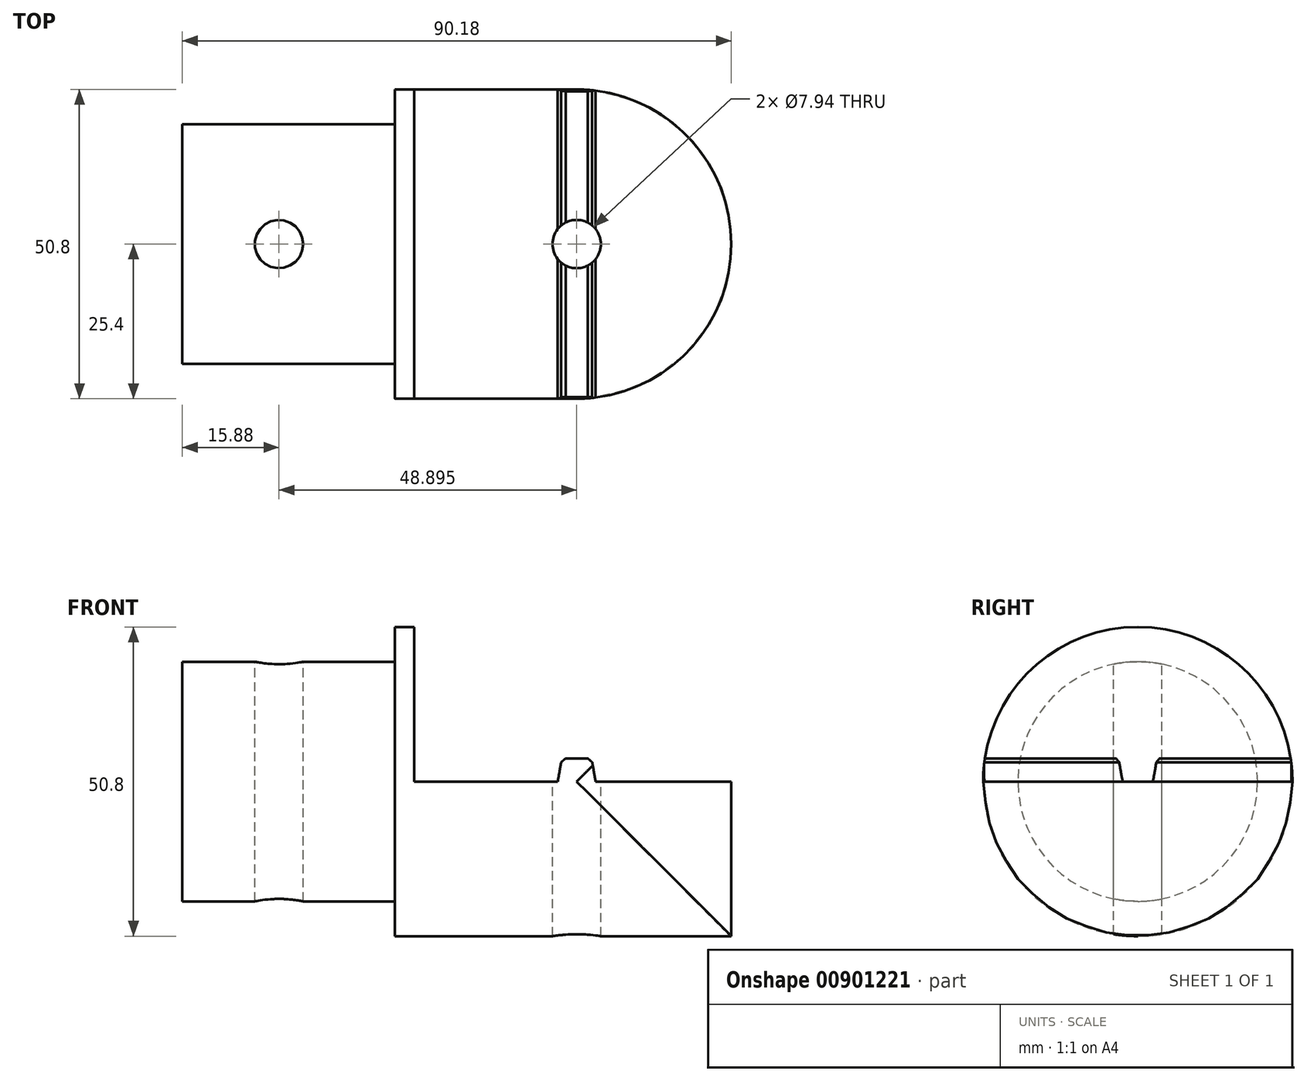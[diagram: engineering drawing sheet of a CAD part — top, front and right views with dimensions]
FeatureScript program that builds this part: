
annotation { "Feature Type Name" : "Feature", "Feature Type Description" : "" }
export const myFeature = defineFeature(function(context is Context, id is Id, definition is map)
    precondition{}
    {
        {
            var Q0;
            Q0=qCreatedBy(makeId("Right.planeOp"),FACE);
            var sketch = newSketch(context, id + "F0", { "sketchPlane" : qUnion([Q0])});
            skCircle(sketch, "E0", {"center": v(0, 0) * mm, "radius": 25.4 * mm});
            skSolve(sketch);
        }
        {
            var Q0;
            Q0=makeQuery(id+"F0.imprint","IMPRINT",FACE,{"disambiguationData":[TD([[makeQuery(id+"F0.imprint","IMPRINT",EDGE,{"derivedFrom":sQuery(id+"F0.wireOp",EDGE,"E0")}),1.0]])]});
            var Q1;
            Q1=sQuery(id+"F0.wireOp",EDGE,"E0");
            extrude(context, id + "F1", {"entities" : qUnion([Q0]), "surfaceEntities" : qUnion([Q1]), "depth" : 3.17 * mm, "offsetDistance" : 25.4 * mm});
        }
        {
            var Q0;
            Q0=makeQuery(id+"F1.opExtrude","CAP_FACE",FACE,{"disambiguationData":[OSD([sQuery(id+"F0.wireOp",EDGE,"E0")])],"isStart":false});
            var sketch = newSketch(context, id + "F2", { "sketchPlane" : qUnion([Q0])});
            skCircle(sketch, "E1", {"center": v(0, 0) * mm, "radius": 19.69 * mm});
            skSolve(sketch);
        }
        {
            var Q0;
            Q0=qSketchRegion(id+"F2",true);
            extrude(context, id + "F3", {"entities" : qUnion([Q0]), "operationType" : NewBodyOperationType.ADD, "oppositeDirection" : true, "depth" : 38.1 * mm, "offsetDistance" : 25.4 * mm});
        }
        {
            var Q0;
            Q0=qCreatedBy(makeId("Right.planeOp"),FACE);
            var sketch = newSketch(context, id + "F4", { "sketchPlane" : qUnion([Q0])});
            skArc(sketch, "E2.0", {"start": v(-25.4, 0) * mm, "mid": v(0, -25.4) * mm, "end": v(25.4, 0) * mm});
            skLineSegment(sketch, "E3", {"start": v(-25.4, 0) * mm, "end": v(25.4, 0) * mm});
            skSolve(sketch);
        }
        {
            var Q0;
            Q0 = qSketchRegion(id + "F4", true);
            extrude(context, id + "F5", {"entities" : qUnion([Q0]), "operationType" : NewBodyOperationType.ADD, "depth" : 58.42 * mm, "offsetDistance" : 25.4 * mm});
        }
        {
            var Q0;
            Q0=makeQuery(id+"F1.opExtrude","CAP_FACE",FACE,{"disambiguationData":[OSD([sQuery(id+"F0.wireOp",EDGE,"E0")])],"isStart":false});
            cPlane(context, id + "F6", {"entities" : qUnion([Q0]), "cplaneType" : CPlaneType.OFFSET, "offset" : 26.67 * mm, "width" : 152.4 * mm, "height" : 152.4 * mm});
        }
        {
            var Q0;
            Q0=qCreatedBy(makeId("Front.planeOp"),FACE);
            var sketch = newSketch(context, id + "F7", { "sketchPlane" : qUnion([Q0])});
            skLineSegment(sketch, "E4", {"start": v(29.84, 54.74) * mm, "end": v(29.85, -54.74) * mm, "construction": true});
            skLineSegment(sketch, "E5.left", {"start": v(32.96, 0) * mm, "end": v(26.73, 0) * mm});
            skLineSegment(sketch, "E5.right", {"start": v(32.28, 3.81) * mm, "end": v(27.4, 3.81) * mm});
            skLineSegment(sketch, "E6", {"start": v(32.96, 0) * mm, "end": v(32.28, 3.8) * mm});
            skLineSegment(sketch, "E7", {"start": v(26.73, 0) * mm, "end": v(27.4, 3.8) * mm});
            skSolve(sketch);
        }
        {
            var Q0;
            Q0=qSketchRegion(id+"F7",true);
            var Q1;
            Q1=makeQuery(id+"F1GSwWC16j8S8zG_1.boolean.opBoolean","MERGE",FACE,{"derivedFrom":[makeQuery(id+"F1.opExtrude","CAP_FACE",FACE,{"disambiguationData":[OSD([sQuery(id+"F0.wireOp",EDGE,"E0")])],"isStart":false})],"fromTools":[makeQuery(id+"F1GSwWC16j8S8zG_1.opExtrude","SWEPT_FACE",FACE,{"disambiguationData":[OSD([sQuery(id+"Fo2Aks5cWjRStkX_1.wireOp",EDGE,"LD30eS7f-A7DZ-0PzW-ksg2-Q8TgDjSmhPE0.left")])]})]});
            extrude(context, id + "F8", {"entities" : qUnion([Q0]), "operationType" : NewBodyOperationType.ADD, "endBound" : BoundingType.SYMMETRIC, "oppositeDirection" : true, "depth" : 50.8 * mm, "endBoundEntityFace" : qUnion([Q1]), "offsetDistance" : 25.4 * mm});
        }
        {
            var Q0;
            Q0=makeQuery(id+"F1.opExtrude","CAP_FACE",FACE,{"disambiguationData":[OSD([sQuery(id+"F0.wireOp",EDGE,"E0")])],"isStart":false});
            var sketch = newSketch(context, id + "F9", { "sketchPlane" : qUnion([Q0])});
            skArc(sketch, "E8", {"start": v(25.4, 0) * mm, "mid": v(0, 25.4) * mm, "end": v(-25.4, 0) * mm});
            skLineSegment(sketch, "E9", {"start": v(-25.4, 0) * mm, "end": v(-30.5, 0) * mm});
            skLineSegment(sketch, "E10", {"start": v(-30.5, 0) * mm, "end": v(-30.5, 28.85) * mm});
            skLineSegment(sketch, "E11", {"start": v(-30.5, 28.85) * mm, "end": v(30.5, 28.85) * mm});
            skLineSegment(sketch, "E12", {"start": v(30.5, 28.85) * mm, "end": v(30.5, 0) * mm});
            skLineSegment(sketch, "E13", {"start": v(25.4, 0) * mm, "end": v(30.5, 0) * mm});
            skSolve(sketch);
        }
        {
            var Q0;
            Q0 = qSketchRegion(id + "F9", true);
            extrude(context, id + "F10", {"entities" : qUnion([Q0]), "operationType" : NewBodyOperationType.REMOVE, "depth" : 50.8 * mm, "offsetDistance" : 25.4 * mm});
        }
        {
            var Q0;
            Q0=makeQuery(id+"F8.opExtrude","SWEPT_EDGE",EDGE,{"disambiguationData":[OSD([sQuery(id+"F7.wireOp",EDGE,"E5.right"),sQuery(id+"F7.wireOp",EDGE,"E6")])]});
            var Q1;
            Q1=makeQuery(id+"F8.opExtrude","SWEPT_EDGE",EDGE,{"disambiguationData":[OSD([sQuery(id+"F7.wireOp",EDGE,"E5.right"),sQuery(id+"F7.wireOp",EDGE,"E7")])]});
            chamfer(context, id + "F11", {"entities" : qUnion([Q0, Q1]), "width" : 0.76 * mm});
        }
        {
            var Q0;
            Q0=qCreatedBy(makeId("Top.planeOp"),FACE);
            cPlane(context, id + "F12", {"entities" : qUnion([Q0]), "cplaneType" : CPlaneType.OFFSET, "offset" : 25.4 * mm, "width" : 152.4 * mm, "height" : 152.4 * mm});
        }
        {
            var Q0;
            Q0=qCreatedBy(id+"F12.planeOp",FACE);
            var sketch = newSketch(context, id + "F13", { "sketchPlane" : qUnion([Q0])});
            skPoint(sketch, "E14", {"position": v(29.85, 0) * mm});
            skPoint(sketch, "E15", {"position": v(29.84, 25.4) * mm});
            skPoint(sketch, "E16", {"position": v(29.85, -25.4) * mm});
            skArc(sketch, "E17", {"start": v(29.85, -25.4) * mm, "mid": v(55.25, 0) * mm, "end": v(29.85, 25.4) * mm});
            skLineSegment(sketch, "E18", {"start": v(29.85, -25.4) * mm, "end": v(29.85, -30.23) * mm});
            skLineSegment(sketch, "E19", {"start": v(29.85, -30.23) * mm, "end": v(58.42, -30.23) * mm});
            skLineSegment(sketch, "E20", {"start": v(58.42, -30.23) * mm, "end": v(58.42, 31.14) * mm});
            skLineSegment(sketch, "E21", {"start": v(58.42, 31.14) * mm, "end": v(29.84, 31.14) * mm});
            skLineSegment(sketch, "E22", {"start": v(29.84, 31.14) * mm, "end": v(29.84, 25.4) * mm});
            skLineSegment(sketch, "E23", {"start": v(29.84, 33.97) * mm, "end": v(29.85, -31.5) * mm, "construction": true});
            skSolve(sketch);
        }
        {
            var Q0;
            Q0=qSketchRegion(id+"F13",true);
            extrude(context, id + "F14", {"entities" : qUnion([Q0]), "operationType" : NewBodyOperationType.REMOVE, "endBound" : BoundingType.THROUGH_ALL, "oppositeDirection" : true, "depth" : 25.4 * mm, "offsetDistance" : 25.4 * mm});
        }
        {
            var Q0;
            Q0=qCreatedBy(id+"F12.planeOp",FACE);
            var sketch = newSketch(context, id + "F15", { "sketchPlane" : qUnion([Q0])});
            skPoint(sketch, "E24", {"position": v(29.85, 0) * mm});
            skPoint(sketch, "E25", {"position": v(-19.05, 0) * mm});
            skSolve(sketch);
        }
        {
            var Q0;
            Q0=sQuery(id+"F15.wireOp",VERTEX,"E25");
            var Q1;
            Q1=sQuery(id+"F15.wireOp",VERTEX,"E24");
            var Q2;
            Q2=makeQuery(id+"F1.opExtrude","SWEPT_BODY",BODY,{"disambiguationData":[OSD([sQuery(id+"F0.wireOp",EDGE,"E0")])]});
            hole(context, id + "F16", {"style" : HoleStyle.SIMPLE, "endStyle" : HoleEndStyle.THROUGH, "standardTappedOrClearance" : lookupTablePath({ "standard" : "ANSI", "engagement" : "75%", "pitch" : "16 tpi", "size" : "3/8", "type" : "Tapped" }), "standardBlindInLast" : lookupTablePath({ "standard" : "ANSI", "engagement" : "75%", "pitch" : "16 tpi", "size" : "3/8", "type" : "Tapped" }), "holeDiameter" : 7.94 * mm, "majorDiameter" : 9.52 * mm, "showTappedDepth" : true, "isTappedThrough" : true, "tappedDepth" : 12.7 * mm, "tapClearance" : 3, "locations" : qUnion([Q0, Q1]), "scope" : qUnion([Q2])});
        }
    });
